# Revit family: P190780JX-159c_JVR0430HS_StainlessSteel_JA_Cooking_Ventilation
name_source: partatom
category: Specialty Equipment
units: mm (PartAtom-declared; Revit-internal decimal feet)

## family parameters
Always vertical = Yes
Cut with Voids When Loaded = No
Enable Cutting in Views = No
Maintain Annotation Orientation = No
Part Type = Normal
Room Calculation Point = No
Round Connector Dimension = Use Diameter
Shared = No
Work Plane-Based = No

## types (1)
- JVR0430HS
    Accent Material = ARCAT - Metal - Steel - Gray
    Amps = 0 A
    Body Material = ARCAT - Metal - Steel - Stainless
    Default Elevation = 0"
    Depth = 17 15/16"
    Description = Lustre Stainless 30" Recirculating Wall-Mount Canopy Hood
Hotte murale à recirculation, 30 po
    Family Name = WALL HOODS - 30"
    Feature 1 = Sonic Hush
Un silence sonique
    Feature 2 = Cylindric Charcoal Refinement
Filtre cylindrique à charbon
    Feature 3 = Emotive Controls
Commandes sensibles
    Height = 2 3/8"
    Installation-Fabrication = http://access.whirlpool.com Instruction&sku=JVR0430HS&language=EN
http://access.whirlpool.com Instruction&sku=JVR0430HS&language=EN
    Manufacturer = Jenn Air
    Model = JVR0430HS
    Vent Material = ARCAT - Metal - Steel - Gray
    Voltage = 0 V
    Width = 29 15/16"

## geometry (parser evidence)
native form markers: Sweep x5
no freeform markers — native parametric forms only
